# Revit family: Sanitary_Showers_hansgrohe_26699XXX-Ecostat-Shower-system-for-expos5
name_source: partatom
category: Plumbing Fixtures
revit_build: Autodesk Revit 2018 (Build: 20170223_1515(x64)
units: mm (PartAtom-declared; Revit-internal decimal feet)

## family parameters
Always vertical = No
Cut with Voids When Loaded = No
OmniClass Number = 23.31.17.00
Part Type = Normal
Room Calculation Point = No
Round Connector Dimension = Use Diameter
Shared = No
Work Plane-Based = Yes

## types (1)
- 400 White/Chrome
    BIMobject category = Showers
    Default Elevation = 4' - 0"
    Design country = Germany
    EAN code = 4059625295595
    Edition number = 1
    GTIN code = https://4059625295595
    IFC Classification = Sanitary Terminal
    Installation instructions = https://www.hansgrohe.com
    Manufacturer country = Germany
    Manufacturer name = hansgrohe
    OmniClass Code = 23-31 17 00
    OmniClass Description = Showers
    Product Guid = 642ab748-b5a4-4ce1-9dc4-e40d1ff80e20
    Product SKU = 26699XXX
    Product data url = https://www.bimobject.com
    Product family = Ecostat
    Product group = Shower combination
    Product name = 26699XXX Ecostat Shower system for exposed installation Vario with Ecostat 1001 CL bath thermostat and shower bar 65 cm Nordic-DZR
    Product url = https://www.hansgrohe.com
    QR code = https://www.bimobject.com
    Technical description = https://www.hansgrohe.com
    UNSPSC Code = 30181503
    Uniclass 1.4 Code = L7214
    Uniclass 1.4 Description = Showers
    Uniclass 2015 Code = SL_35_80_80
    Uniclass 2015 Name = Showers
    Weight Net (Kg) = 3.1

## geometry (parser evidence)
native form markers: Sweep x2
no freeform markers — native parametric forms only
